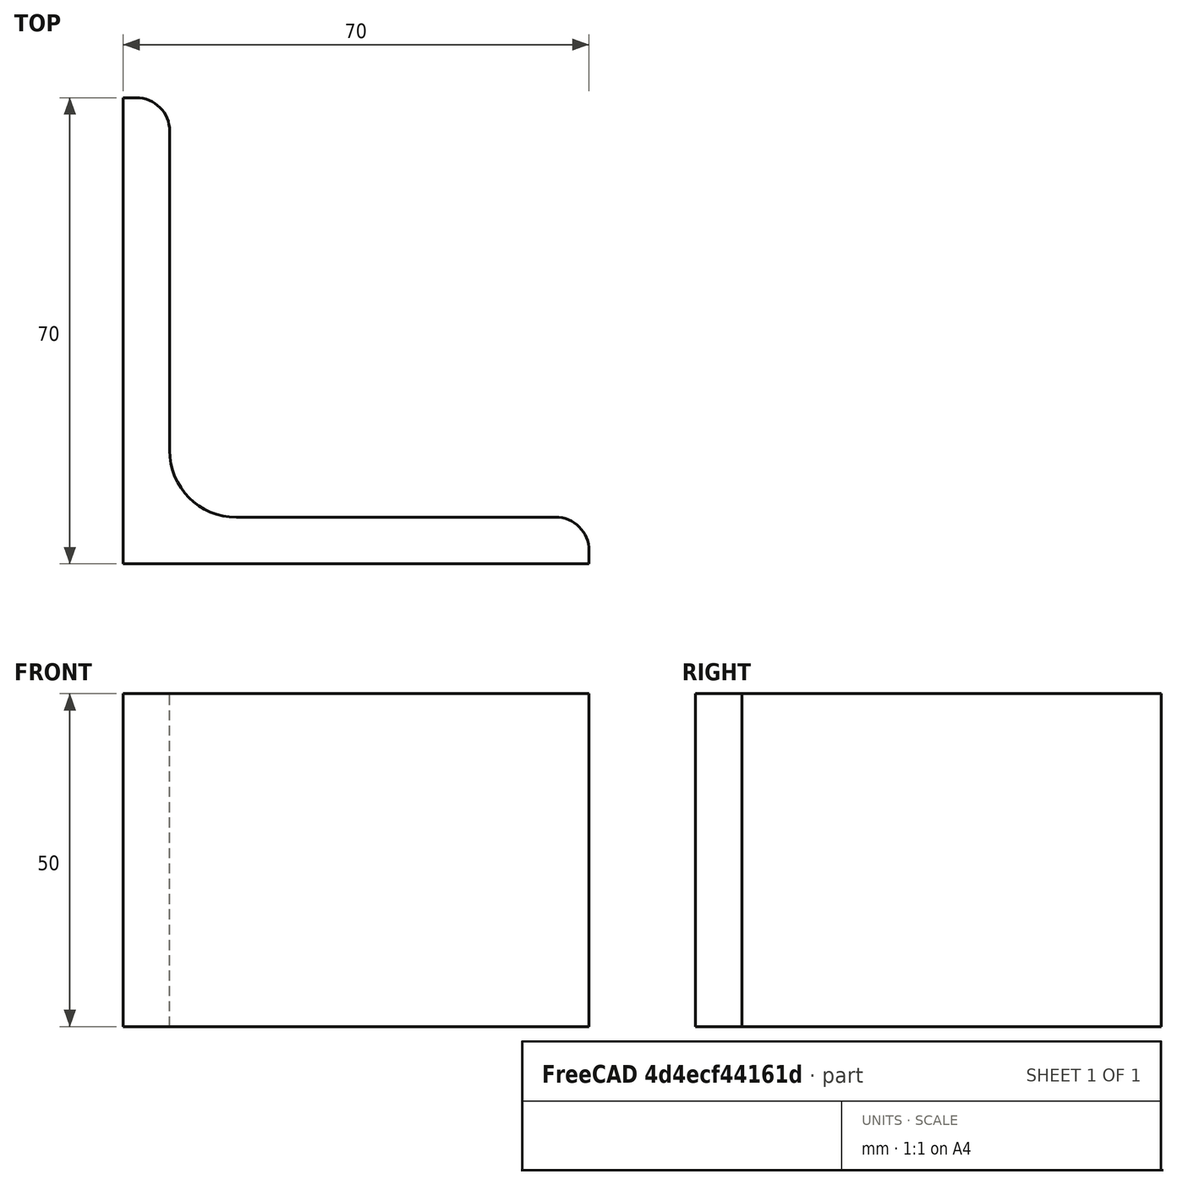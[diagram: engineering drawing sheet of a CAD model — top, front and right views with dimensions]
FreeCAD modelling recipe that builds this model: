
FCSTD DOCUMENT  (FreeCAD 0.15R4671 (Git))
Label: Angle Bar L70x70x7 EN10056 S235JR
License: All rights reserved
LicenseURL: http://en.wikipedia.org/wiki/All_rights_reserved
objects: Sketcher::SketchObject×1, Part::Extrusion×1
note: 2 computed .brp shape members not serialized (recipe doc carries the construction recipe); baked Part::Feature solids carry a one-line shape summary decoded from their .brp

FEATURE [Sketcher::SketchObject] Sketch
  sketch-geometry (9):
    g0: LineSegment StartX=0 StartY=0 StartZ=0 EndX=70 EndY=0 EndZ=0
    g1: LineSegment StartX=70 StartY=0 StartZ=0 EndX=70 EndY=2 EndZ=0
    g2: LineSegment StartX=65 StartY=7 StartZ=0 EndX=17 EndY=7 EndZ=0
    g3: LineSegment StartX=0 StartY=0 StartZ=0 EndX=0 EndY=70 EndZ=0
    g4: LineSegment StartX=0 StartY=70 StartZ=0 EndX=2 EndY=70 EndZ=0
    g5: LineSegment StartX=7 StartY=65 StartZ=0 EndX=7 EndY=17 EndZ=0
    g6: ArcOfCircle CenterX=17 CenterY=17 CenterZ=0 NormalX=0 NormalY=0 NormalZ=1 Radius=10 StartAngle=3.14159 EndAngle=4.71239
    g7: ArcOfCircle CenterX=2 CenterY=65 CenterZ=0 NormalX=0 NormalY=0 NormalZ=1 Radius=5 StartAngle=0 EndAngle=1.5708
    g8: ArcOfCircle CenterX=65 CenterY=2 CenterZ=0 NormalX=0 NormalY=0 NormalZ=1 Radius=5 StartAngle=0 EndAngle=1.5708
  constraints (23):
    c: Coincident(g0,g-1)
    c: Horizontal(g0)
    c: Coincident(g1,g0)
    c: Vertical(g1)
    c: Horizontal(g2)
    c: Coincident(g3,g-1)
    c: Vertical(g3)
    c: Coincident(g4,g3)
    c: Horizontal(g4)
    c: Vertical(g5)
    c: Tangent(g5,g6) = -1.5708
    c: Tangent(g2,g6) = 1.5708
    c: Tangent(g4,g7) = 1.5708
    c: Tangent(g5,g7) = 1.5708
    c: Tangent(g2,g8) = -1.5708
    c: Tangent(g1,g8) = -1.5708
    c: DistanceX(g0) = 70
    c: DistanceY(g3) = 70
    c: DistanceY(g0,g2) = 7
    c: DistanceX(g3,g5) = 7
    c: Radius(g6) = 10
    c: Radius(g8) = 5
    c: Radius(g7) = 5
FEATURE [Part::Extrusion] Extrude  label="Angle Bar L70x70x7 EN10056 S235JR"
  Base = -> Sketch
  Dir = (0,0,50)
  Solid = true
